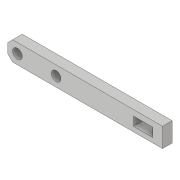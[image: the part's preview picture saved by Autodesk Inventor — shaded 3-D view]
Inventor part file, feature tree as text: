
AUTODESK INVENTOR PART (.ipt)
format: ipt  version: 2017 (Build 210142000, 142)  size: 95,232 bytes
history: native  units: in
note: dims shown in document units (in); Inventor stores cm internally (conversion verified against a paired STEP export)
features: extrude x1, chamfer x1, sketch x1
ambient origin geometry x8: Origin, YZ Plane, XZ Plane, XY Plane, X Axis, Y Axis, Z Axis, Center Point
bodies: Solid1 (feature_tree)
feature tree (3):
  extrude  "Extrusion1"  Depth=0.25in
  chamfer  "Chamfer1"  Distance=0.125in
  sketch  "Sketch1"  dims[d0=2.0in d1=0.25in d2=0.125in d3=0.125in d4=0.125in d5=0.125in d6=0.125in d7=0.5in d8=0.115in d9=0.0625in d10=0.25in d11=0.125in d12=0.125in d13=0.0in d14=0.0625in d15=0.125in d16=45.0deg]
